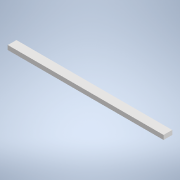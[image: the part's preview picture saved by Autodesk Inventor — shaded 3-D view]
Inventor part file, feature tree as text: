
AUTODESK INVENTOR PART (.ipt)
format: ipt  version: 2022 (Build 260153000, 153)  size: 95,232 bytes
history: native  units: in
note: dims shown in document units (in); Inventor stores cm internally (conversion verified against a paired STEP export)
features: plane x1, extrude x1, sketch x1
ambient origin geometry x8: Origin, YZ Plane, XZ Plane, XY Plane, X Axis, Y Axis, Z Axis, Center Point
bodies: Solid1 (feature_tree)
feature tree (3):
  plane  "Work Plane1"
  extrude  "Extrusion1"  Depth=1.0in
  sketch  "Sketch1"  dims[d0=18.0in d1=1.0in d2=0.5in d3=0.0in d4=0.5in d5=0.0344in d6=0.5in d7=0.0344in]
